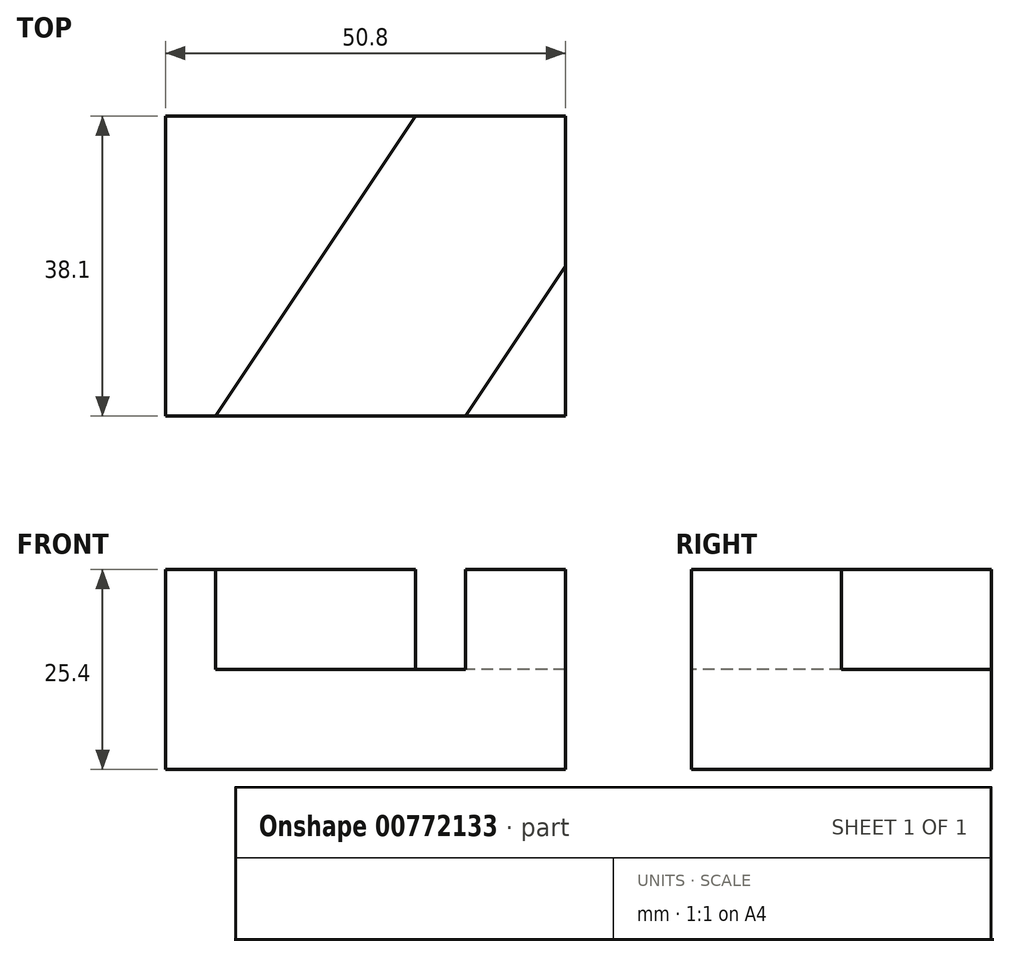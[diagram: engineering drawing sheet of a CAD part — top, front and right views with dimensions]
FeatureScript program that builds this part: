
annotation { "Feature Type Name" : "Feature", "Feature Type Description" : "" }
export const myFeature = defineFeature(function(context is Context, id is Id, definition is map)
    precondition{}
    {
        {
            var Q0;
            Q0=qCreatedBy(makeId("Front.planeOp"),FACE);
            var sketch = newSketch(context, id + "F0", { "sketchPlane" : qUnion([Q0])});
            skLineSegment(sketch, "E0", {"start": v(0, 0) * mm, "end": v(50.8, 0) * mm});
            skLineSegment(sketch, "E1", {"start": v(50.8, 0) * mm, "end": v(50.8, 25.4) * mm});
            skLineSegment(sketch, "E2", {"start": v(50.8, 25.4) * mm, "end": v(0, 25.4) * mm});
            skLineSegment(sketch, "E3", {"start": v(0, 25.4) * mm, "end": v(0, 0) * mm});
            skSolve(sketch);
        }
        {
            var Q0;
            Q0 = qSketchRegion(id + "F0", true);
            extrude(context, id + "F1", {"entities" : qUnion([Q0]), "depth" : 38.1 * mm, "offsetDistance" : 25.4 * mm});
        }
        {
            var Q0;
            Q0=makeQuery(id+"F1.opExtrude","SWEPT_FACE",FACE,{"disambiguationData":[OSD([sQuery(id+"F0.wireOp",EDGE,"E2")])]});
            var sketch = newSketch(context, id + "F2", { "sketchPlane" : qUnion([Q0])});
            skLineSegment(sketch, "E4", {"start": v(50.8, -38.1) * mm, "end": v(38.1, -38.1) * mm});
            skLineSegment(sketch, "E5", {"start": v(50.8, -38.1) * mm, "end": v(50.8, -19.05) * mm});
            skLineSegment(sketch, "E6", {"start": v(50.8, -19.05) * mm, "end": v(38.1, -38.1) * mm});
            skLineSegment(sketch, "E7", {"start": v(0, -38.1) * mm, "end": v(6.35, -38.1) * mm});
            skLineSegment(sketch, "E8", {"start": v(0, 0) * mm, "end": v(31.75, 0) * mm});
            skLineSegment(sketch, "E9", {"start": v(31.75, 0) * mm, "end": v(6.35, -38.1) * mm});
            skSolve(sketch);
        }
        {
            var Q0;
            {var subQ5=sQuery(id+"F2.wireOp",EDGE,"E6");Q0=makeQuery(id+"F2.imprint","IMPRINT",FACE,{"disambiguationData":[TD([[makeQuery(id+"F2.imprint","IMPRINT",EDGE,{"derivedFrom":subQ5}),-1.0]])]});}
            extrude(context, id + "F3", {"entities" : qUnion([Q0]), "operationType" : NewBodyOperationType.REMOVE, "oppositeDirection" : true, "depth" : 12.7 * mm, "offsetDistance" : 25.4 * mm});
        }
    });
